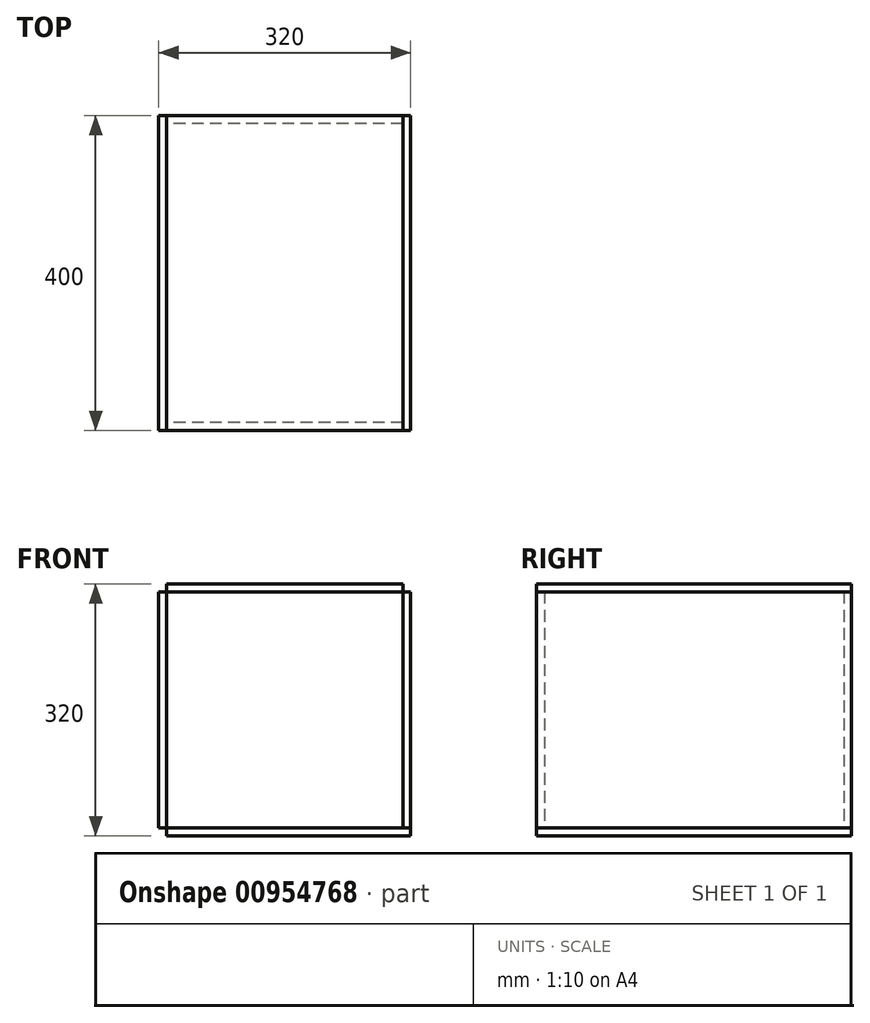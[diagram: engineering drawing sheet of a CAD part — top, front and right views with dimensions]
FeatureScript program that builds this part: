
annotation { "Feature Type Name" : "Feature", "Feature Type Description" : "" }
export const myFeature = defineFeature(function(context is Context, id is Id, definition is map)
    precondition{}
    {
        {
            var Q0;
            Q0=qCreatedBy(makeId("Right.planeOp"),FACE);
            var sketch = newSketch(context, id + "F0", { "sketchPlane" : qUnion([Q0])});
            skLineSegment(sketch, "E0.bottom", {"start": v(-200, 150) * mm, "end": v(200, 150) * mm});
            skLineSegment(sketch, "E0.top", {"start": v(-200, -150) * mm, "end": v(200, -150) * mm});
            skLineSegment(sketch, "E0.left", {"start": v(-200, 150) * mm, "end": v(-200, -150) * mm});
            skLineSegment(sketch, "E0.right", {"start": v(200, 150) * mm, "end": v(200, -150) * mm});
            skPoint(sketch, "E0.middle", {"position": v(0, 0) * mm});
            skSolve(sketch);
        }
        {
            var Q0;
            Q0=makeQuery(id+"F0.imprint","IMPRINT",FACE,{"disambiguationData":[TD([[makeQuery(id+"F0.imprint","IMPRINT",EDGE,{"derivedFrom":sQuery(id+"F0.wireOp",EDGE,"E0.bottom")}),-1.0]])]});
            extrude(context, id + "F1", {"entities" : qUnion([Q0]), "depth" : 10 * mm, "offsetDistance" : 25 * mm});
        }
        {
            var Q0;
            Q0=makeQuery(id+"F1.opExtrude","SWEPT_FACE",FACE,{"disambiguationData":[OSD([sQuery(id+"F0.wireOp",EDGE,"E0.left")])]});
            var sketch = newSketch(context, id + "F2", { "sketchPlane" : qUnion([Q0])});
            skLineSegment(sketch, "E1.bottom", {"start": v(0, -150) * mm, "end": v(-300, -150) * mm});
            skLineSegment(sketch, "E1.top", {"start": v(0, 150) * mm, "end": v(-300, 150) * mm});
            skLineSegment(sketch, "E1.left", {"start": v(0, -150) * mm, "end": v(0, 150) * mm});
            skLineSegment(sketch, "E1.right", {"start": v(-300, -150) * mm, "end": v(-300, 150) * mm});
            skSolve(sketch);
        }
        {
            var Q0;
            Q0=makeQuery(id+"F2.imprint","IMPRINT",FACE,{"disambiguationData":[TD([[makeQuery(id+"F2.imprint","IMPRINT",EDGE,{"derivedFrom":sQuery(id+"F2.wireOp",EDGE,"E1.bottom")}),-1.0]])]});
            extrude(context, id + "F3", {"entities" : qUnion([Q0]), "oppositeDirection" : true, "depth" : 10 * mm, "offsetDistance" : 25 * mm});
        }
        {
            var Q0;
            Q0=makeQuery(id+"F3.opExtrude","SWEPT_BODY",BODY,{"disambiguationData":[OSD([sQuery(id+"F2.wireOp",EDGE,"E1.bottom"),sQuery(id+"F2.wireOp",EDGE,"E1.top"),sQuery(id+"F2.wireOp",EDGE,"E1.left"),sQuery(id+"F2.wireOp",EDGE,"E1.right")])]});
            var Q1;
            Q1=qCreatedBy(makeId("Front.planeOp"),FACE);
            mirror(context, id + "F4", {"entities" : qUnion([Q0]), "mirrorPlane" : qUnion([Q1])});
        }
        {
            var Q0;
            Q0=makeQuery(id+"F1.opExtrude","CAP_FACE",FACE,{"disambiguationData":[OSD([sQuery(id+"F0.wireOp",EDGE,"E0.bottom"),sQuery(id+"F0.wireOp",EDGE,"E0.top"),sQuery(id+"F0.wireOp",EDGE,"E0.left"),sQuery(id+"F0.wireOp",EDGE,"E0.right")])],"isStart":true});
            cPlane(context, id + "F5", {"entities" : qUnion([Q0]), "cplaneType" : CPlaneType.OFFSET, "offset" : 150 * mm, "width" : 150 * mm, "height" : 150 * mm});
        }
        {
            var Q0;
            Q0=makeQuery(id+"F1.opExtrude","SWEPT_BODY",BODY,{"disambiguationData":[OSD([sQuery(id+"F0.wireOp",EDGE,"E0.bottom"),sQuery(id+"F0.wireOp",EDGE,"E0.top"),sQuery(id+"F0.wireOp",EDGE,"E0.left"),sQuery(id+"F0.wireOp",EDGE,"E0.right")])]});
            var Q1;
            Q1=qCreatedBy(id+"F5.planeOp",FACE);
            mirror(context, id + "F6", {"entities" : qUnion([Q0]), "mirrorPlane" : qUnion([Q1])});
        }
        {
            var Q0;
            Q0=makeQuery(id+"F6.opPattern","COPY",FACE,{"derivedFrom":makeQuery(id+"F1.opExtrude","SWEPT_FACE",FACE,{"disambiguationData":[OSD([sQuery(id+"F0.wireOp",EDGE,"E0.bottom")])]}),"instanceName":"1"});
            var sketch = newSketch(context, id + "F7", { "sketchPlane" : qUnion([Q0])});
            skLineSegment(sketch, "E2.bottom", {"start": v(0, -200) * mm, "end": v(-300, -200) * mm});
            skLineSegment(sketch, "E2.top", {"start": v(0, 200) * mm, "end": v(-300, 200) * mm});
            skLineSegment(sketch, "E2.left", {"start": v(0, -200) * mm, "end": v(0, 200) * mm});
            skLineSegment(sketch, "E2.right", {"start": v(-300, -200) * mm, "end": v(-300, 200) * mm});
            skSolve(sketch);
        }
        {
            var Q0;
            Q0=makeQuery(id+"F7.imprint","IMPRINT",FACE,{"disambiguationData":[TD([[makeQuery(id+"F7.imprint","IMPRINT",EDGE,{"derivedFrom":sQuery(id+"F7.wireOp",EDGE,"E2.bottom")}),-1.0]])]});
            extrude(context, id + "F8", {"entities" : qUnion([Q0]), "depth" : 10 * mm, "offsetDistance" : 25 * mm});
        }
        {
            var Q0;
            Q0=makeQuery(id+"F6.opPattern","COPY",FACE,{"derivedFrom":makeQuery(id+"F1.opExtrude","SWEPT_FACE",FACE,{"disambiguationData":[OSD([sQuery(id+"F0.wireOp",EDGE,"E0.top")])]}),"instanceName":"1"});
            var sketch = newSketch(context, id + "F9", { "sketchPlane" : qUnion([Q0])});
            skLineSegment(sketch, "E3.bottom", {"start": v(-310, 200) * mm, "end": v(10, 200) * mm});
            skLineSegment(sketch, "E3.top", {"start": v(-310, -200) * mm, "end": v(10, -200) * mm});
            skLineSegment(sketch, "E3.left", {"start": v(-310, 200) * mm, "end": v(-310, -200) * mm});
            skLineSegment(sketch, "E3.right", {"start": v(10, 200) * mm, "end": v(10, -200) * mm});
            skSolve(sketch);
        }
        {
            var Q0;
            {var subQ2=sQuery(id+"F9.wireOp",EDGE,"E3.right");Q0=makeQuery(id+"F9.imprint","IMPRINT",FACE,{"disambiguationData":[TD([[makeQuery(id+"F9.imprint","IMPRINT",EDGE,{"derivedFrom":subQ2}),-1.0]])]});}
            extrude(context, id + "F10", {"entities" : qUnion([Q0]), "depth" : 10 * mm, "offsetDistance" : 25 * mm});
        }
    });
